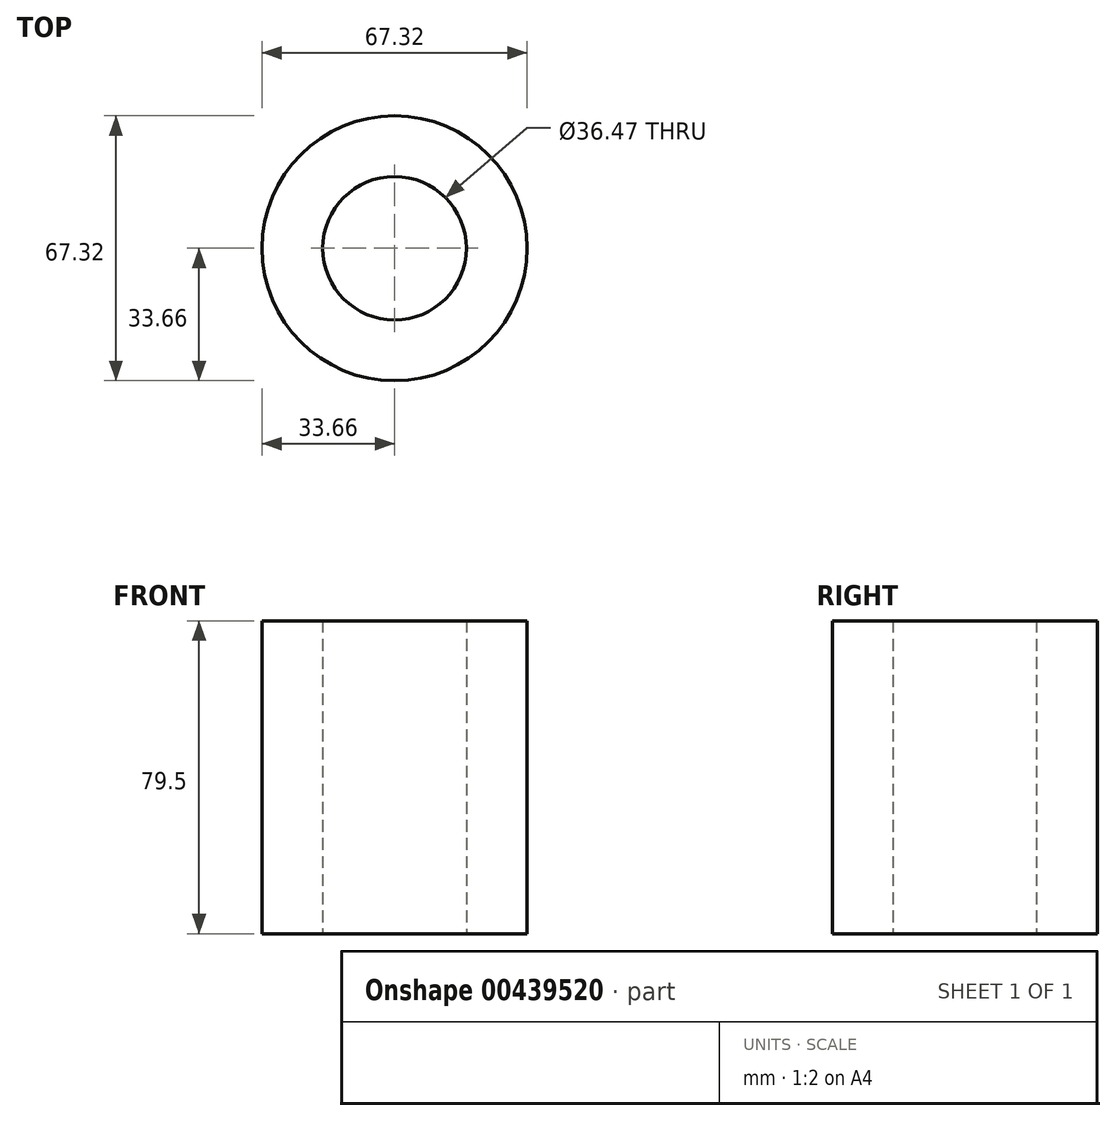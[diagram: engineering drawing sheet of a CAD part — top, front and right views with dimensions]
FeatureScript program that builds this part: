
annotation { "Feature Type Name" : "Feature", "Feature Type Description" : "" }
export const myFeature = defineFeature(function(context is Context, id is Id, definition is map)
    precondition{}
    {
        {
            var Q0;
            Q0=qCreatedBy(makeId("Top.planeOp"),FACE);
            var sketch = newSketch(context, id + "F0", { "sketchPlane" : qUnion([Q0])});
            skCircle(sketch, "E0", {"center": v(0, 0) * mm, "radius": 33.66 * mm});
            skCircle(sketch, "E1", {"center": v(0, 0) * mm, "radius": 18.24 * mm});
            skSolve(sketch);
        }
        {
            var Q0;
            Q0=makeQuery(id+"F0.imprint","IMPRINT",FACE,{"disambiguationData":[TD([[makeQuery(id+"F0.imprint","IMPRINT",EDGE,{"derivedFrom":sQuery(id+"F0.wireOp",EDGE,"E0")}),1.0]])]});
            extrude(context, id + "F1", {"entities" : qUnion([Q0]), "depth" : 79.5 * mm});
        }
    });
